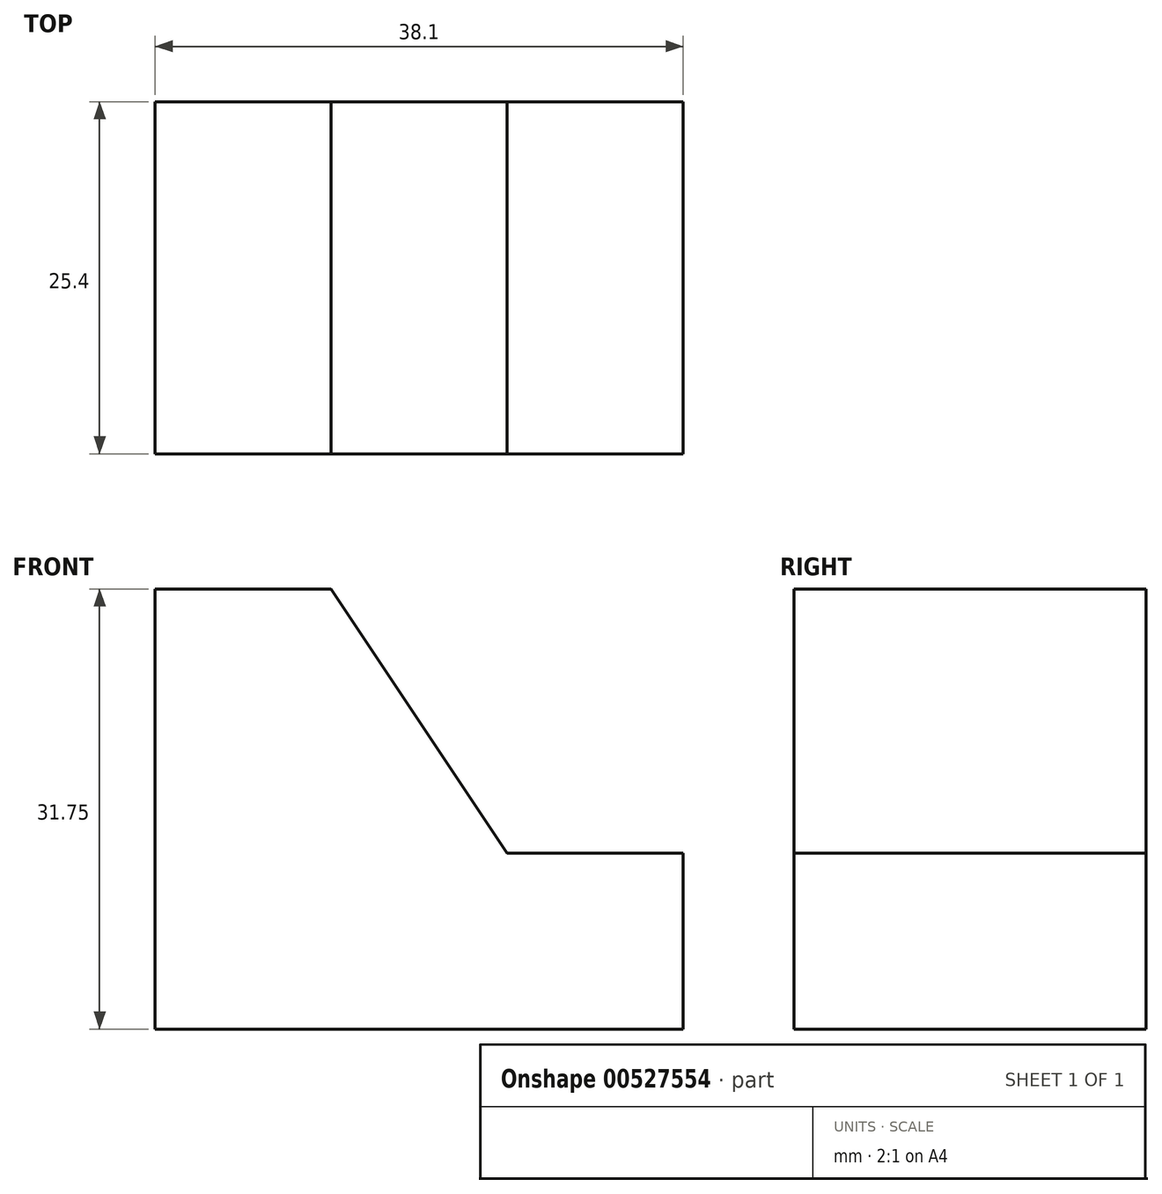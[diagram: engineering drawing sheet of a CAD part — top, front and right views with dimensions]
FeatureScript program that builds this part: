
annotation { "Feature Type Name" : "Feature", "Feature Type Description" : "" }
export const myFeature = defineFeature(function(context is Context, id is Id, definition is map)
    precondition{}
    {
        {
            var Q0;
            Q0=qCreatedBy(makeId("Front.planeOp"),FACE);
            var sketch = newSketch(context, id + "F0", { "sketchPlane" : qUnion([Q0])});
            skLineSegment(sketch, "E0", {"start": v(0, 0) * mm, "end": v(0, 31.75) * mm});
            skLineSegment(sketch, "E1", {"start": v(0, 31.75) * mm, "end": v(12.7, 31.75) * mm});
            skLineSegment(sketch, "E2", {"start": v(38.1, 12.7) * mm, "end": v(38.1, 0) * mm});
            skLineSegment(sketch, "E3", {"start": v(38.1, 0) * mm, "end": v(0, 0) * mm});
            skLineSegment(sketch, "E4", {"start": v(38.1, 12.7) * mm, "end": v(25.4, 12.7) * mm});
            skLineSegment(sketch, "E5", {"start": v(25.4, 12.7) * mm, "end": v(12.7, 31.75) * mm});
            skSolve(sketch);
        }
        {
            var Q0;
            Q0=makeQuery(id+"F0.imprint","IMPRINT",FACE,{"disambiguationData":[TD([[makeQuery(id+"F0.imprint","IMPRINT",EDGE,{"derivedFrom":sQuery(id+"F0.wireOp",EDGE,"E0")}),-1.0]])]});
            extrude(context, id + "F1", {"entities" : qUnion([Q0]), "depth" : 25.4 * mm, "offsetDistance" : 25.4 * mm});
        }
    });
